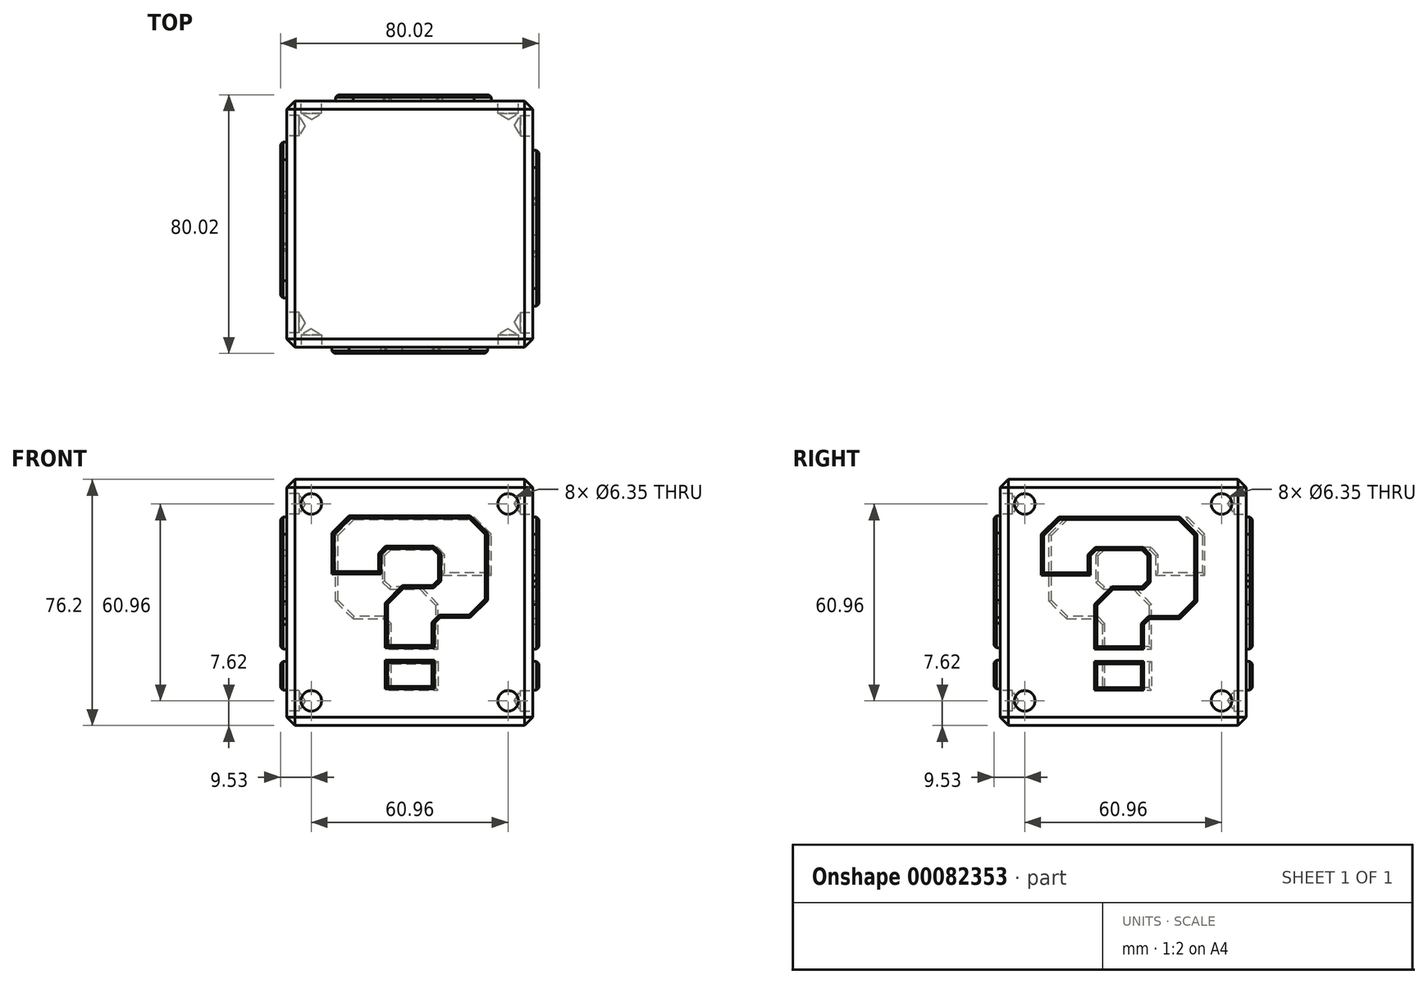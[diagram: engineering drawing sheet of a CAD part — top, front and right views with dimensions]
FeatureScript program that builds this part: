
annotation { "Feature Type Name" : "Feature", "Feature Type Description" : "" }
export const myFeature = defineFeature(function(context is Context, id is Id, definition is map)
    precondition{}
    {
        {
            var Q0;
            Q0=qCreatedBy(makeId("Front.planeOp"),FACE);
            var sketch = newSketch(context, id + "F17", { "sketchPlane" : qUnion([Q0])});
            skLineSegment(sketch, "E0.bottom", {"start": v(38.1, -38.1) * mm, "end": v(-38.1, -38.1) * mm});
            skLineSegment(sketch, "E0.top", {"start": v(38.1, 38.1) * mm, "end": v(-38.1, 38.1) * mm});
            skLineSegment(sketch, "E0.left", {"start": v(38.1, -38.1) * mm, "end": v(38.1, 38.1) * mm});
            skLineSegment(sketch, "E0.right", {"start": v(-38.1, -38.1) * mm, "end": v(-38.1, 38.1) * mm});
            skPoint(sketch, "E0.middle", {"position": v(0, 0) * mm});
            skSolve(sketch);
        }
        {
            var Q0;
            Q0=makeQuery(id+"F17.imprint","IMPRINT",FACE,{"disambiguationData":[TD([[makeQuery(id+"F17.imprint","IMPRINT",EDGE,{"derivedFrom":sQuery(id+"F17.wireOp",EDGE,"E0.bottom")}),-1.0]])]});
            extrude(context, id + "F0", {"entities" : qUnion([Q0]), "endBound" : BoundingType.SYMMETRIC, "depth" : 76.2 * mm});
        }
        {
            var Q0;
            Q0=makeQuery(id+"F0.opExtrude","SWEPT_FACE",FACE,{"disambiguationData":[OSD([sQuery(id+"F17.wireOp",EDGE,"E0.top")])]});
            var Q1;
            Q1=makeQuery(id+"F0.opExtrude","SWEPT_FACE",FACE,{"disambiguationData":[OSD([sQuery(id+"F17.wireOp",EDGE,"E0.left")])]});
            var Q2;
            Q2=makeQuery(id+"F0.opExtrude","CAP_FACE",FACE,{"disambiguationData":[OSD([sQuery(id+"F17.wireOp",EDGE,"E0.bottom"),sQuery(id+"F17.wireOp",EDGE,"E0.top"),sQuery(id+"F17.wireOp",EDGE,"E0.left"),sQuery(id+"F17.wireOp",EDGE,"E0.right")])],"isStart":false});
            var Q3;
            Q3=makeQuery(id+"F0.opExtrude","CAP_FACE",FACE,{"disambiguationData":[OSD([sQuery(id+"F17.wireOp",EDGE,"E0.bottom"),sQuery(id+"F17.wireOp",EDGE,"E0.top"),sQuery(id+"F17.wireOp",EDGE,"E0.left"),sQuery(id+"F17.wireOp",EDGE,"E0.right")])],"isStart":true});
            var Q4;
            Q4=makeQuery(id+"F0.opExtrude","SWEPT_FACE",FACE,{"disambiguationData":[OSD([sQuery(id+"F17.wireOp",EDGE,"E0.right")])]});
            var Q5;
            Q5=makeQuery(id+"F0.opExtrude","SWEPT_FACE",FACE,{"disambiguationData":[OSD([sQuery(id+"F17.wireOp",EDGE,"E0.bottom")])]});
            chamfer(context, id + "F1", {"entities" : qUnion([Q0, Q1, Q2, Q3, Q4, Q5]), "width" : 2.54 * mm, "tangentPropagation" : true});
        }
        {
            var Q0;
            Q0=makeQuery(id+"F0.opExtrude","CAP_FACE",FACE,{"disambiguationData":[OSD([sQuery(id+"F17.wireOp",EDGE,"E0.bottom"),sQuery(id+"F17.wireOp",EDGE,"E0.top"),sQuery(id+"F17.wireOp",EDGE,"E0.left"),sQuery(id+"F17.wireOp",EDGE,"E0.right")])],"isStart":false});
            var sketch = newSketch(context, id + "F18", { "sketchPlane" : qUnion([Q0])});
            skPoint(sketch, "E1", {"position": v(30.48, 30.48) * mm});
            skPoint(sketch, "E2", {"position": v(30.48, -30.48) * mm});
            skPoint(sketch, "E3", {"position": v(-30.48, -30.48) * mm});
            skPoint(sketch, "E4", {"position": v(-30.48, 30.48) * mm});
            skSolve(sketch);
        }
        {
            var Q0;
            Q0=sQuery(id+"F18.wireOp",VERTEX,"E4");
            var Q1;
            Q1=sQuery(id+"F18.wireOp",VERTEX,"E1");
            var Q2;
            Q2=sQuery(id+"F18.wireOp",VERTEX,"E2");
            var Q3;
            Q3=sQuery(id+"F18.wireOp",VERTEX,"E3");
            var Q4;
            Q4=makeQuery(id+"F0.opExtrude","SWEPT_BODY",BODY,{"disambiguationData":[OSD([sQuery(id+"F17.wireOp",EDGE,"E0.bottom"),sQuery(id+"F17.wireOp",EDGE,"E0.top"),sQuery(id+"F17.wireOp",EDGE,"E0.left"),sQuery(id+"F17.wireOp",EDGE,"E0.right")])]});
            hole(context, id + "F2", {"style" : HoleStyle.SIMPLE, "endStyle" : HoleEndStyle.BLIND, "holeDiameter" : 6.35 * mm, "holeDepth" : 3.8 * mm, "locations" : qUnion([Q0, Q1, Q2, Q3]), "scope" : qUnion([Q4])});
        }
        {
            var Q0;
            Q0=makeQuery(id+"F0.opExtrude","SWEPT_FACE",FACE,{"disambiguationData":[OSD([sQuery(id+"F17.wireOp",EDGE,"E0.left")])]});
            var sketch = newSketch(context, id + "F19", { "sketchPlane" : qUnion([Q0])});
            skPoint(sketch, "E5", {"position": v(30.48, 30.48) * mm});
            skPoint(sketch, "E6", {"position": v(30.48, -30.48) * mm});
            skPoint(sketch, "E7", {"position": v(-30.48, -30.48) * mm});
            skPoint(sketch, "E8", {"position": v(-30.48, 30.48) * mm});
            skLineSegment(sketch, "E9.bottom", {"start": v(6.4, -18.33) * mm, "end": v(-8.84, -18.33) * mm});
            skLineSegment(sketch, "E9.top", {"start": v(6.4, -27.22) * mm, "end": v(-8.84, -27.22) * mm});
            skLineSegment(sketch, "E9.left", {"start": v(6.4, -18.33) * mm, "end": v(6.4, -27.22) * mm});
            skLineSegment(sketch, "E9.right", {"start": v(-8.84, -18.33) * mm, "end": v(-8.84, -27.22) * mm});
            skPoint(sketch, "E9.middle", {"position": v(-1.22, -22.77) * mm});
            skLineSegment(sketch, "E10", {"start": v(-8.84, -14.52) * mm, "end": v(-8.84, -14.52) * mm});
            skLineSegment(sketch, "E11", {"start": v(-8.84, -14.52) * mm, "end": v(-8.84, -0.58) * mm});
            skLineSegment(sketch, "E12", {"start": v(5.87, 16.27) * mm, "end": v(-8.32, 16.27) * mm});
            skLineSegment(sketch, "E13", {"start": v(-10.11, 14.47) * mm, "end": v(-10.11, 8.34) * mm});
            skLineSegment(sketch, "E14", {"start": v(-10.11, 8.34) * mm, "end": v(-25.35, 8.34) * mm});
            skLineSegment(sketch, "E15", {"start": v(-25.35, 8.34) * mm, "end": v(-25.35, 21.04) * mm});
            skLineSegment(sketch, "E16", {"start": v(-25.35, 21.04) * mm, "end": v(-19.96, 26.43) * mm});
            skLineSegment(sketch, "E17", {"start": v(17.52, 26.43) * mm, "end": v(22.9, 21.04) * mm});
            skLineSegment(sketch, "E18", {"start": v(17.52, -5.1) * mm, "end": v(8.2, -5.1) * mm});
            skLineSegment(sketch, "E19", {"start": v(6.4, -6.9) * mm, "end": v(6.4, -14.52) * mm});
            skLineSegment(sketch, "E20", {"start": v(6.4, -14.52) * mm, "end": v(6.4, -14.52) * mm});
            skLineSegment(sketch, "E21", {"start": v(6.4, -14.52) * mm, "end": v(-8.84, -14.52) * mm});
            skLineSegment(sketch, "E22", {"start": v(-8.84, -0.58) * mm, "end": v(-3.45, 4.8) * mm});
            skLineSegment(sketch, "E23", {"start": v(17.52, -5.1) * mm, "end": v(22.9, 0.29) * mm});
            skLineSegment(sketch, "E24", {"start": v(22.9, 0.29) * mm, "end": v(22.9, 21.04) * mm});
            skLineSegment(sketch, "E25", {"start": v(-3.45, 4.8) * mm, "end": v(5.87, 4.8) * mm});
            skLineSegment(sketch, "E26", {"start": v(5.87, 4.8) * mm, "end": v(7.67, 6.6) * mm});
            skLineSegment(sketch, "E27", {"start": v(7.67, 6.6) * mm, "end": v(7.67, 14.47) * mm});
            skLineSegment(sketch, "E28", {"start": v(17.52, 26.43) * mm, "end": v(-19.96, 26.43) * mm});
            skLineSegment(sketch, "E29", {"start": v(-10.11, 14.47) * mm, "end": v(-8.32, 16.27) * mm});
            skLineSegment(sketch, "E30", {"start": v(7.67, 14.47) * mm, "end": v(5.87, 16.27) * mm});
            skLineSegment(sketch, "E31", {"start": v(6.4, -6.9) * mm, "end": v(8.2, -5.1) * mm});
            skSolve(sketch);
        }
        {
            var Q0;
            Q0=sQuery(id+"F19.wireOp",VERTEX,"E8");
            var Q1;
            Q1=sQuery(id+"F19.wireOp",VERTEX,"E5");
            var Q2;
            Q2=sQuery(id+"F19.wireOp",VERTEX,"E6");
            var Q3;
            Q3=sQuery(id+"F19.wireOp",VERTEX,"E7");
            var Q4;
            Q4=makeQuery(id+"F0.opExtrude","SWEPT_BODY",BODY,{"disambiguationData":[OSD([sQuery(id+"F17.wireOp",EDGE,"E0.bottom"),sQuery(id+"F17.wireOp",EDGE,"E0.top"),sQuery(id+"F17.wireOp",EDGE,"E0.left"),sQuery(id+"F17.wireOp",EDGE,"E0.right")])]});
            hole(context, id + "F3", {"style" : HoleStyle.SIMPLE, "endStyle" : HoleEndStyle.BLIND, "holeDiameter" : 6.35 * mm, "holeDepth" : 3.8 * mm, "locations" : qUnion([Q0, Q1, Q2, Q3]), "scope" : qUnion([Q4])});
        }
        {
            var Q0;
            Q0=makeQuery(id+"F0.opExtrude","CAP_FACE",FACE,{"disambiguationData":[OSD([sQuery(id+"F17.wireOp",EDGE,"E0.bottom"),sQuery(id+"F17.wireOp",EDGE,"E0.top"),sQuery(id+"F17.wireOp",EDGE,"E0.left"),sQuery(id+"F17.wireOp",EDGE,"E0.right")])],"isStart":true});
            var sketch = newSketch(context, id + "F4", { "sketchPlane" : qUnion([Q0])});
            skPoint(sketch, "E32", {"position": v(-30.48, 30.48) * mm});
            skPoint(sketch, "E33", {"position": v(30.48, 30.48) * mm});
            skPoint(sketch, "E34", {"position": v(30.48, -30.48) * mm});
            skPoint(sketch, "E35", {"position": v(-30.48, -30.48) * mm});
            skLineSegment(sketch, "E36.bottom", {"start": v(6.4, -18.33) * mm, "end": v(-8.84, -18.33) * mm});
            skLineSegment(sketch, "E36.top", {"start": v(6.4, -27.22) * mm, "end": v(-8.84, -27.22) * mm});
            skLineSegment(sketch, "E36.left", {"start": v(6.4, -18.33) * mm, "end": v(6.4, -27.22) * mm});
            skLineSegment(sketch, "E36.right", {"start": v(-8.84, -18.33) * mm, "end": v(-8.84, -27.22) * mm});
            skPoint(sketch, "E36.middle", {"position": v(-1.22, -22.77) * mm});
            skLineSegment(sketch, "E37", {"start": v(-8.84, -14.52) * mm, "end": v(-8.84, -14.52) * mm});
            skLineSegment(sketch, "E38", {"start": v(-8.84, -14.52) * mm, "end": v(-8.84, -0.58) * mm});
            skLineSegment(sketch, "E39", {"start": v(5.87, 16.27) * mm, "end": v(-8.32, 16.27) * mm});
            skLineSegment(sketch, "E40", {"start": v(-10.11, 14.47) * mm, "end": v(-10.11, 8.34) * mm});
            skLineSegment(sketch, "E41", {"start": v(-10.11, 8.34) * mm, "end": v(-25.35, 8.34) * mm});
            skLineSegment(sketch, "E42", {"start": v(-25.35, 8.34) * mm, "end": v(-25.35, 21.04) * mm});
            skLineSegment(sketch, "E43", {"start": v(-25.35, 21.04) * mm, "end": v(-19.96, 26.43) * mm});
            skLineSegment(sketch, "E44", {"start": v(17.52, 26.43) * mm, "end": v(22.9, 21.04) * mm});
            skLineSegment(sketch, "E45", {"start": v(17.52, -5.1) * mm, "end": v(8.2, -5.1) * mm});
            skLineSegment(sketch, "E46", {"start": v(6.4, -6.9) * mm, "end": v(6.4, -14.52) * mm});
            skLineSegment(sketch, "E47", {"start": v(6.4, -14.52) * mm, "end": v(6.4, -14.52) * mm});
            skLineSegment(sketch, "E48", {"start": v(6.4, -14.52) * mm, "end": v(-8.84, -14.52) * mm});
            skLineSegment(sketch, "E49", {"start": v(-8.84, -0.58) * mm, "end": v(-3.45, 4.8) * mm});
            skLineSegment(sketch, "E50", {"start": v(17.52, -5.1) * mm, "end": v(22.9, 0.29) * mm});
            skLineSegment(sketch, "E51", {"start": v(22.9, 0.29) * mm, "end": v(22.9, 21.04) * mm});
            skLineSegment(sketch, "E52", {"start": v(-3.45, 4.8) * mm, "end": v(5.87, 4.8) * mm});
            skLineSegment(sketch, "E53", {"start": v(5.87, 4.8) * mm, "end": v(7.67, 6.6) * mm});
            skLineSegment(sketch, "E54", {"start": v(7.67, 6.6) * mm, "end": v(7.67, 14.47) * mm});
            skLineSegment(sketch, "E55", {"start": v(17.52, 26.43) * mm, "end": v(-19.96, 26.43) * mm});
            skLineSegment(sketch, "E56", {"start": v(-10.11, 14.47) * mm, "end": v(-8.32, 16.27) * mm});
            skLineSegment(sketch, "E57", {"start": v(7.67, 14.47) * mm, "end": v(5.87, 16.27) * mm});
            skLineSegment(sketch, "E58", {"start": v(6.4, -6.9) * mm, "end": v(8.2, -5.1) * mm});
            skSolve(sketch);
        }
        {
            var Q0;
            Q0=sQuery(id+"F4.wireOp",VERTEX,"E32");
            var Q1;
            Q1=sQuery(id+"F4.wireOp",VERTEX,"E33");
            var Q2;
            Q2=sQuery(id+"F4.wireOp",VERTEX,"E34");
            var Q3;
            Q3=sQuery(id+"F4.wireOp",VERTEX,"E35");
            var Q4;
            Q4=makeQuery(id+"F0.opExtrude","SWEPT_BODY",BODY,{"disambiguationData":[OSD([sQuery(id+"F17.wireOp",EDGE,"E0.bottom"),sQuery(id+"F17.wireOp",EDGE,"E0.top"),sQuery(id+"F17.wireOp",EDGE,"E0.left"),sQuery(id+"F17.wireOp",EDGE,"E0.right")])]});
            hole(context, id + "F5", {"style" : HoleStyle.SIMPLE, "endStyle" : HoleEndStyle.BLIND, "holeDiameter" : 6.35 * mm, "holeDepth" : 3.8 * mm, "locations" : qUnion([Q0, Q1, Q2, Q3]), "scope" : qUnion([Q4])});
        }
        {
            var Q0;
            Q0=makeQuery(id+"F0.opExtrude","SWEPT_FACE",FACE,{"disambiguationData":[OSD([sQuery(id+"F17.wireOp",EDGE,"E0.right")])]});
            var sketch = newSketch(context, id + "F6", { "sketchPlane" : qUnion([Q0])});
            skPoint(sketch, "E59", {"position": v(-30.48, 30.48) * mm});
            skPoint(sketch, "E60", {"position": v(30.48, 30.48) * mm});
            skPoint(sketch, "E61", {"position": v(30.48, -30.48) * mm});
            skPoint(sketch, "E62", {"position": v(-30.48, -30.48) * mm});
            skLineSegment(sketch, "E63.bottom", {"start": v(6.4, -18.33) * mm, "end": v(-8.84, -18.33) * mm});
            skLineSegment(sketch, "E63.top", {"start": v(6.4, -27.22) * mm, "end": v(-8.84, -27.22) * mm});
            skLineSegment(sketch, "E63.left", {"start": v(6.4, -18.33) * mm, "end": v(6.4, -27.22) * mm});
            skLineSegment(sketch, "E63.right", {"start": v(-8.84, -18.33) * mm, "end": v(-8.84, -27.22) * mm});
            skPoint(sketch, "E63.middle", {"position": v(-1.22, -22.77) * mm});
            skLineSegment(sketch, "E64", {"start": v(-8.84, -14.52) * mm, "end": v(-8.84, -14.52) * mm});
            skLineSegment(sketch, "E65", {"start": v(-8.84, -14.52) * mm, "end": v(-8.84, -0.58) * mm});
            skLineSegment(sketch, "E66", {"start": v(5.87, 16.27) * mm, "end": v(-8.32, 16.27) * mm});
            skLineSegment(sketch, "E67", {"start": v(-10.11, 14.47) * mm, "end": v(-10.11, 8.34) * mm});
            skLineSegment(sketch, "E68", {"start": v(-10.11, 8.34) * mm, "end": v(-25.35, 8.34) * mm});
            skLineSegment(sketch, "E69", {"start": v(-25.35, 8.34) * mm, "end": v(-25.35, 21.04) * mm});
            skLineSegment(sketch, "E70", {"start": v(-25.35, 21.04) * mm, "end": v(-19.96, 26.43) * mm});
            skLineSegment(sketch, "E71", {"start": v(17.52, 26.43) * mm, "end": v(22.9, 21.04) * mm});
            skLineSegment(sketch, "E72", {"start": v(17.52, -5.1) * mm, "end": v(8.2, -5.1) * mm});
            skLineSegment(sketch, "E73", {"start": v(6.4, -6.9) * mm, "end": v(6.4, -14.52) * mm});
            skLineSegment(sketch, "E74", {"start": v(6.4, -14.52) * mm, "end": v(6.4, -14.52) * mm});
            skLineSegment(sketch, "E75", {"start": v(6.4, -14.52) * mm, "end": v(-8.84, -14.52) * mm});
            skLineSegment(sketch, "E76", {"start": v(-8.84, -0.58) * mm, "end": v(-3.45, 4.8) * mm});
            skLineSegment(sketch, "E77", {"start": v(17.52, -5.1) * mm, "end": v(22.9, 0.29) * mm});
            skLineSegment(sketch, "E78", {"start": v(22.9, 0.29) * mm, "end": v(22.9, 21.04) * mm});
            skLineSegment(sketch, "E79", {"start": v(-3.45, 4.8) * mm, "end": v(5.87, 4.8) * mm});
            skLineSegment(sketch, "E80", {"start": v(5.87, 4.8) * mm, "end": v(7.67, 6.6) * mm});
            skLineSegment(sketch, "E81", {"start": v(7.67, 6.6) * mm, "end": v(7.67, 14.47) * mm});
            skLineSegment(sketch, "E82", {"start": v(17.52, 26.43) * mm, "end": v(-19.96, 26.43) * mm});
            skLineSegment(sketch, "E83", {"start": v(-10.11, 14.47) * mm, "end": v(-8.32, 16.27) * mm});
            skLineSegment(sketch, "E84", {"start": v(7.67, 14.47) * mm, "end": v(5.87, 16.27) * mm});
            skLineSegment(sketch, "E85", {"start": v(6.4, -6.9) * mm, "end": v(8.2, -5.1) * mm});
            skSolve(sketch);
        }
        {
            var Q0;
            Q0=sQuery(id+"F6.wireOp",VERTEX,"E59");
            var Q1;
            Q1=sQuery(id+"F6.wireOp",VERTEX,"E60");
            var Q2;
            Q2=sQuery(id+"F6.wireOp",VERTEX,"E61");
            var Q3;
            Q3=sQuery(id+"F6.wireOp",VERTEX,"E62");
            var Q4;
            Q4=makeQuery(id+"F0.opExtrude","SWEPT_BODY",BODY,{"disambiguationData":[OSD([sQuery(id+"F17.wireOp",EDGE,"E0.bottom"),sQuery(id+"F17.wireOp",EDGE,"E0.top"),sQuery(id+"F17.wireOp",EDGE,"E0.left"),sQuery(id+"F17.wireOp",EDGE,"E0.right")])]});
            hole(context, id + "F7", {"style" : HoleStyle.SIMPLE, "endStyle" : HoleEndStyle.BLIND, "holeDiameter" : 6.35 * mm, "holeDepth" : 3.8 * mm, "locations" : qUnion([Q0, Q1, Q2, Q3]), "scope" : qUnion([Q4])});
        }
        {
            var Q0;
            Q0=makeQuery(id+"F0.opExtrude","CAP_FACE",FACE,{"disambiguationData":[OSD([sQuery(id+"F17.wireOp",EDGE,"E0.bottom"),sQuery(id+"F17.wireOp",EDGE,"E0.top"),sQuery(id+"F17.wireOp",EDGE,"E0.left"),sQuery(id+"F17.wireOp",EDGE,"E0.right")])],"isStart":false});
            var sketch = newSketch(context, id + "F8", { "sketchPlane" : qUnion([Q0])});
            skLineSegment(sketch, "E86.bottom", {"start": v(7.62, -17.93) * mm, "end": v(-7.62, -17.93) * mm});
            skLineSegment(sketch, "E86.top", {"start": v(7.62, -26.82) * mm, "end": v(-7.62, -26.82) * mm});
            skLineSegment(sketch, "E86.left", {"start": v(7.62, -17.93) * mm, "end": v(7.62, -26.82) * mm});
            skLineSegment(sketch, "E86.right", {"start": v(-7.62, -17.93) * mm, "end": v(-7.62, -26.82) * mm});
            skPoint(sketch, "E86.middle", {"position": v(0, -22.38) * mm});
            skLineSegment(sketch, "E87", {"start": v(-7.62, -14.12) * mm, "end": v(-7.62, -14.12) * mm});
            skLineSegment(sketch, "E88", {"start": v(-7.62, -14.12) * mm, "end": v(-7.62, -0.19) * mm});
            skLineSegment(sketch, "E89", {"start": v(7.1, 16.67) * mm, "end": v(-7.1, 16.67) * mm});
            skLineSegment(sketch, "E90", {"start": v(-8.89, 14.87) * mm, "end": v(-8.89, 8.74) * mm});
            skLineSegment(sketch, "E91", {"start": v(-8.89, 8.74) * mm, "end": v(-24.13, 8.74) * mm});
            skLineSegment(sketch, "E92", {"start": v(-24.13, 8.74) * mm, "end": v(-24.13, 21.44) * mm});
            skLineSegment(sketch, "E93", {"start": v(-24.13, 21.44) * mm, "end": v(-18.74, 26.83) * mm});
            skLineSegment(sketch, "E94", {"start": v(18.74, 26.83) * mm, "end": v(24.13, 21.44) * mm});
            skLineSegment(sketch, "E95", {"start": v(18.74, -4.7) * mm, "end": v(9.42, -4.7) * mm});
            skLineSegment(sketch, "E96", {"start": v(7.62, -6.5) * mm, "end": v(7.62, -14.12) * mm});
            skLineSegment(sketch, "E97", {"start": v(7.62, -14.12) * mm, "end": v(7.62, -14.12) * mm});
            skLineSegment(sketch, "E98", {"start": v(7.62, -14.12) * mm, "end": v(-7.62, -14.12) * mm});
            skLineSegment(sketch, "E99", {"start": v(-7.62, -0.19) * mm, "end": v(-2.23, 5.2) * mm});
            skLineSegment(sketch, "E100", {"start": v(18.74, -4.7) * mm, "end": v(24.13, 0.68) * mm});
            skLineSegment(sketch, "E101", {"start": v(24.13, 0.68) * mm, "end": v(24.13, 21.44) * mm});
            skLineSegment(sketch, "E102", {"start": v(-2.23, 5.2) * mm, "end": v(7.1, 5.2) * mm});
            skLineSegment(sketch, "E103", {"start": v(7.1, 5.2) * mm, "end": v(8.89, 7) * mm});
            skLineSegment(sketch, "E104", {"start": v(8.89, 7) * mm, "end": v(8.89, 14.87) * mm});
            skLineSegment(sketch, "E105", {"start": v(18.74, 26.83) * mm, "end": v(-18.74, 26.83) * mm});
            skLineSegment(sketch, "E106", {"start": v(-8.9, 14.87) * mm, "end": v(-7.1, 16.67) * mm});
            skLineSegment(sketch, "E107", {"start": v(8.89, 14.87) * mm, "end": v(7.1, 16.67) * mm});
            skLineSegment(sketch, "E108", {"start": v(7.62, -6.5) * mm, "end": v(9.42, -4.7) * mm});
            skSolve(sketch);
        }
        {
            var Q0;
            Q0=makeQuery(id+"F8.imprint","IMPRINT",FACE,{"disambiguationData":[TD([[makeQuery(id+"F8.imprint","IMPRINT",EDGE,{"derivedFrom":sQuery(id+"F8.wireOp",EDGE,"E88")}),-1.0]])]});
            var Q1;
            Q1=makeQuery(id+"F8.imprint","IMPRINT",FACE,{"disambiguationData":[TD([[makeQuery(id+"F8.imprint","IMPRINT",EDGE,{"derivedFrom":sQuery(id+"F8.wireOp",EDGE,"E86.bottom")}),1.0]])]});
            extrude(context, id + "F9", {"entities" : qUnion([Q0, Q1]), "operationType" : NewBodyOperationType.ADD, "depth" : 1.9 * mm});
        }
        {
            var Q0;
            Q0=makeQuery(id+"F9.opExtrude","CAP_FACE",FACE,{"disambiguationData":[OSD([sQuery(id+"F8.wireOp",EDGE,"E88"),sQuery(id+"F8.wireOp",EDGE,"E89"),sQuery(id+"F8.wireOp",EDGE,"E90"),sQuery(id+"F8.wireOp",EDGE,"E91"),sQuery(id+"F8.wireOp",EDGE,"E92"),sQuery(id+"F8.wireOp",EDGE,"E93"),sQuery(id+"F8.wireOp",EDGE,"E94"),sQuery(id+"F8.wireOp",EDGE,"E95"),sQuery(id+"F8.wireOp",EDGE,"E96"),sQuery(id+"F8.wireOp",EDGE,"E98"),sQuery(id+"F8.wireOp",EDGE,"E99"),sQuery(id+"F8.wireOp",EDGE,"E100"),sQuery(id+"F8.wireOp",EDGE,"E101"),sQuery(id+"F8.wireOp",EDGE,"E102"),sQuery(id+"F8.wireOp",EDGE,"E103"),sQuery(id+"F8.wireOp",EDGE,"E104"),sQuery(id+"F8.wireOp",EDGE,"E105"),sQuery(id+"F8.wireOp",EDGE,"E106"),sQuery(id+"F8.wireOp",EDGE,"E107"),sQuery(id+"F8.wireOp",EDGE,"E108")])],"isStart":false});
            var Q1;
            Q1=makeQuery(id+"F9.opExtrude","CAP_FACE",FACE,{"disambiguationData":[OSD([sQuery(id+"F8.wireOp",EDGE,"E86.bottom"),sQuery(id+"F8.wireOp",EDGE,"E86.top"),sQuery(id+"F8.wireOp",EDGE,"E86.left"),sQuery(id+"F8.wireOp",EDGE,"E86.right")])],"isStart":false});
            chamfer(context, id + "F10", {"entities" : qUnion([Q0, Q1]), "width" : 0.76 * mm, "tangentPropagation" : true});
        }
        {
            var Q0;
            Q0=makeQuery(id+"F19.imprint","IMPRINT",FACE,{"disambiguationData":[TD([[makeQuery(id+"F19.imprint","IMPRINT",EDGE,{"derivedFrom":sQuery(id+"F19.wireOp",EDGE,"E11")}),-1.0]])]});
            var Q1;
            Q1=makeQuery(id+"F19.imprint","IMPRINT",FACE,{"disambiguationData":[TD([[makeQuery(id+"F19.imprint","IMPRINT",EDGE,{"derivedFrom":sQuery(id+"F19.wireOp",EDGE,"E9.bottom")}),1.0]])]});
            extrude(context, id + "F11", {"entities" : qUnion([Q0, Q1]), "operationType" : NewBodyOperationType.ADD, "depth" : 1.9 * mm});
        }
        {
            var Q0;
            Q0=makeQuery(id+"F11.opExtrude","CAP_FACE",FACE,{"disambiguationData":[OSD([sQuery(id+"F19.wireOp",EDGE,"E11"),sQuery(id+"F19.wireOp",EDGE,"E12"),sQuery(id+"F19.wireOp",EDGE,"E13"),sQuery(id+"F19.wireOp",EDGE,"E14"),sQuery(id+"F19.wireOp",EDGE,"E15"),sQuery(id+"F19.wireOp",EDGE,"E16"),sQuery(id+"F19.wireOp",EDGE,"E17"),sQuery(id+"F19.wireOp",EDGE,"E18"),sQuery(id+"F19.wireOp",EDGE,"E19"),sQuery(id+"F19.wireOp",EDGE,"E21"),sQuery(id+"F19.wireOp",EDGE,"E22"),sQuery(id+"F19.wireOp",EDGE,"E23"),sQuery(id+"F19.wireOp",EDGE,"E24"),sQuery(id+"F19.wireOp",EDGE,"E25"),sQuery(id+"F19.wireOp",EDGE,"E26"),sQuery(id+"F19.wireOp",EDGE,"E27"),sQuery(id+"F19.wireOp",EDGE,"E28"),sQuery(id+"F19.wireOp",EDGE,"E29"),sQuery(id+"F19.wireOp",EDGE,"E30"),sQuery(id+"F19.wireOp",EDGE,"E31")])],"isStart":false});
            var Q1;
            Q1=makeQuery(id+"F11.opExtrude","CAP_FACE",FACE,{"disambiguationData":[OSD([sQuery(id+"F19.wireOp",EDGE,"E9.bottom"),sQuery(id+"F19.wireOp",EDGE,"E9.top"),sQuery(id+"F19.wireOp",EDGE,"E9.left"),sQuery(id+"F19.wireOp",EDGE,"E9.right")])],"isStart":false});
            chamfer(context, id + "F12", {"entities" : qUnion([Q0, Q1]), "width" : 0.76 * mm, "tangentPropagation" : true});
        }
        {
            var Q0;
            Q0=makeQuery(id+"F4.imprint","IMPRINT",FACE,{"disambiguationData":[TD([[makeQuery(id+"F4.imprint","IMPRINT",EDGE,{"derivedFrom":sQuery(id+"F4.wireOp",EDGE,"E38")}),-1.0]])]});
            var Q1;
            Q1=makeQuery(id+"F4.imprint","IMPRINT",FACE,{"disambiguationData":[TD([[makeQuery(id+"F4.imprint","IMPRINT",EDGE,{"derivedFrom":sQuery(id+"F4.wireOp",EDGE,"E36.bottom")}),1.0]])]});
            extrude(context, id + "F13", {"entities" : qUnion([Q0, Q1]), "operationType" : NewBodyOperationType.ADD, "depth" : 1.9 * mm});
        }
        {
            var Q0;
            Q0=makeQuery(id+"F13.opExtrude","CAP_FACE",FACE,{"disambiguationData":[OSD([sQuery(id+"F4.wireOp",EDGE,"E38"),sQuery(id+"F4.wireOp",EDGE,"E39"),sQuery(id+"F4.wireOp",EDGE,"E40"),sQuery(id+"F4.wireOp",EDGE,"E41"),sQuery(id+"F4.wireOp",EDGE,"E42"),sQuery(id+"F4.wireOp",EDGE,"E43"),sQuery(id+"F4.wireOp",EDGE,"E44"),sQuery(id+"F4.wireOp",EDGE,"E45"),sQuery(id+"F4.wireOp",EDGE,"E46"),sQuery(id+"F4.wireOp",EDGE,"E48"),sQuery(id+"F4.wireOp",EDGE,"E49"),sQuery(id+"F4.wireOp",EDGE,"E50"),sQuery(id+"F4.wireOp",EDGE,"E51"),sQuery(id+"F4.wireOp",EDGE,"E52"),sQuery(id+"F4.wireOp",EDGE,"E53"),sQuery(id+"F4.wireOp",EDGE,"E54"),sQuery(id+"F4.wireOp",EDGE,"E55"),sQuery(id+"F4.wireOp",EDGE,"E56"),sQuery(id+"F4.wireOp",EDGE,"E57"),sQuery(id+"F4.wireOp",EDGE,"E58")])],"isStart":false});
            var Q1;
            Q1=makeQuery(id+"F13.opExtrude","CAP_FACE",FACE,{"disambiguationData":[OSD([sQuery(id+"F4.wireOp",EDGE,"E36.bottom"),sQuery(id+"F4.wireOp",EDGE,"E36.top"),sQuery(id+"F4.wireOp",EDGE,"E36.left"),sQuery(id+"F4.wireOp",EDGE,"E36.right")])],"isStart":false});
            chamfer(context, id + "F14", {"entities" : qUnion([Q0, Q1]), "width" : 0.76 * mm, "tangentPropagation" : true});
        }
        {
            var Q0;
            Q0=makeQuery(id+"F6.imprint","IMPRINT",FACE,{"disambiguationData":[TD([[makeQuery(id+"F6.imprint","IMPRINT",EDGE,{"derivedFrom":sQuery(id+"F6.wireOp",EDGE,"E65")}),-1.0]])]});
            var Q1;
            Q1=makeQuery(id+"F6.imprint","IMPRINT",FACE,{"disambiguationData":[TD([[makeQuery(id+"F6.imprint","IMPRINT",EDGE,{"derivedFrom":sQuery(id+"F6.wireOp",EDGE,"E63.bottom")}),1.0]])]});
            extrude(context, id + "F15", {"entities" : qUnion([Q0, Q1]), "operationType" : NewBodyOperationType.ADD, "depth" : 1.9 * mm});
        }
        {
            var Q0;
            Q0=makeQuery(id+"F15.opExtrude","CAP_FACE",FACE,{"disambiguationData":[OSD([sQuery(id+"F6.wireOp",EDGE,"E65"),sQuery(id+"F6.wireOp",EDGE,"E66"),sQuery(id+"F6.wireOp",EDGE,"E67"),sQuery(id+"F6.wireOp",EDGE,"E68"),sQuery(id+"F6.wireOp",EDGE,"E69"),sQuery(id+"F6.wireOp",EDGE,"E70"),sQuery(id+"F6.wireOp",EDGE,"E71"),sQuery(id+"F6.wireOp",EDGE,"E72"),sQuery(id+"F6.wireOp",EDGE,"E73"),sQuery(id+"F6.wireOp",EDGE,"E75"),sQuery(id+"F6.wireOp",EDGE,"E76"),sQuery(id+"F6.wireOp",EDGE,"E77"),sQuery(id+"F6.wireOp",EDGE,"E78"),sQuery(id+"F6.wireOp",EDGE,"E79"),sQuery(id+"F6.wireOp",EDGE,"E80"),sQuery(id+"F6.wireOp",EDGE,"E81"),sQuery(id+"F6.wireOp",EDGE,"E82"),sQuery(id+"F6.wireOp",EDGE,"E83"),sQuery(id+"F6.wireOp",EDGE,"E84"),sQuery(id+"F6.wireOp",EDGE,"E85")])],"isStart":false});
            var Q1;
            Q1=makeQuery(id+"F15.opExtrude","CAP_FACE",FACE,{"disambiguationData":[OSD([sQuery(id+"F6.wireOp",EDGE,"E63.bottom"),sQuery(id+"F6.wireOp",EDGE,"E63.top"),sQuery(id+"F6.wireOp",EDGE,"E63.left"),sQuery(id+"F6.wireOp",EDGE,"E63.right")])],"isStart":false});
            chamfer(context, id + "F16", {"entities" : qUnion([Q0, Q1]), "width" : 0.76 * mm, "tangentPropagation" : true});
        }
    });
